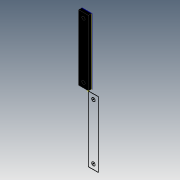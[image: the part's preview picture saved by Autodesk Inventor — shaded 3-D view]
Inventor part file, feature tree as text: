
AUTODESK INVENTOR PART (.ipt)
format: ipt  version: 2015 (Build 190159000, 159)  size: 91,136 bytes
history: native  units: mm
features: other x4, sketch x3, extrude x1, projected_geometry x1
ambient origin geometry x8: Origin, YZ Plane, XZ Plane, XY Plane, X Axis, Y Axis, Z Axis, Center Point
bodies: Solid1 (feature_tree)
feature tree (9):
  other  "Blocks"
  extrude  "Extrusion1"  Depth=200.0mm
  sketch  "Sketch2"  dims[d2=10.0mm]
  sketch  "Sketch3"  dims[d3=10.0mm d4=15.0mm d5=15.0mm d6=10.0mm d7=0.0mm]
  sketch  "Sketch1"  dims[d0=30.0mm d1=200.0mm]
  projected_geometry  "Projected Loop1"
  other  "Block1"
  other  "Block1:1"
  other  "Block1:2"
